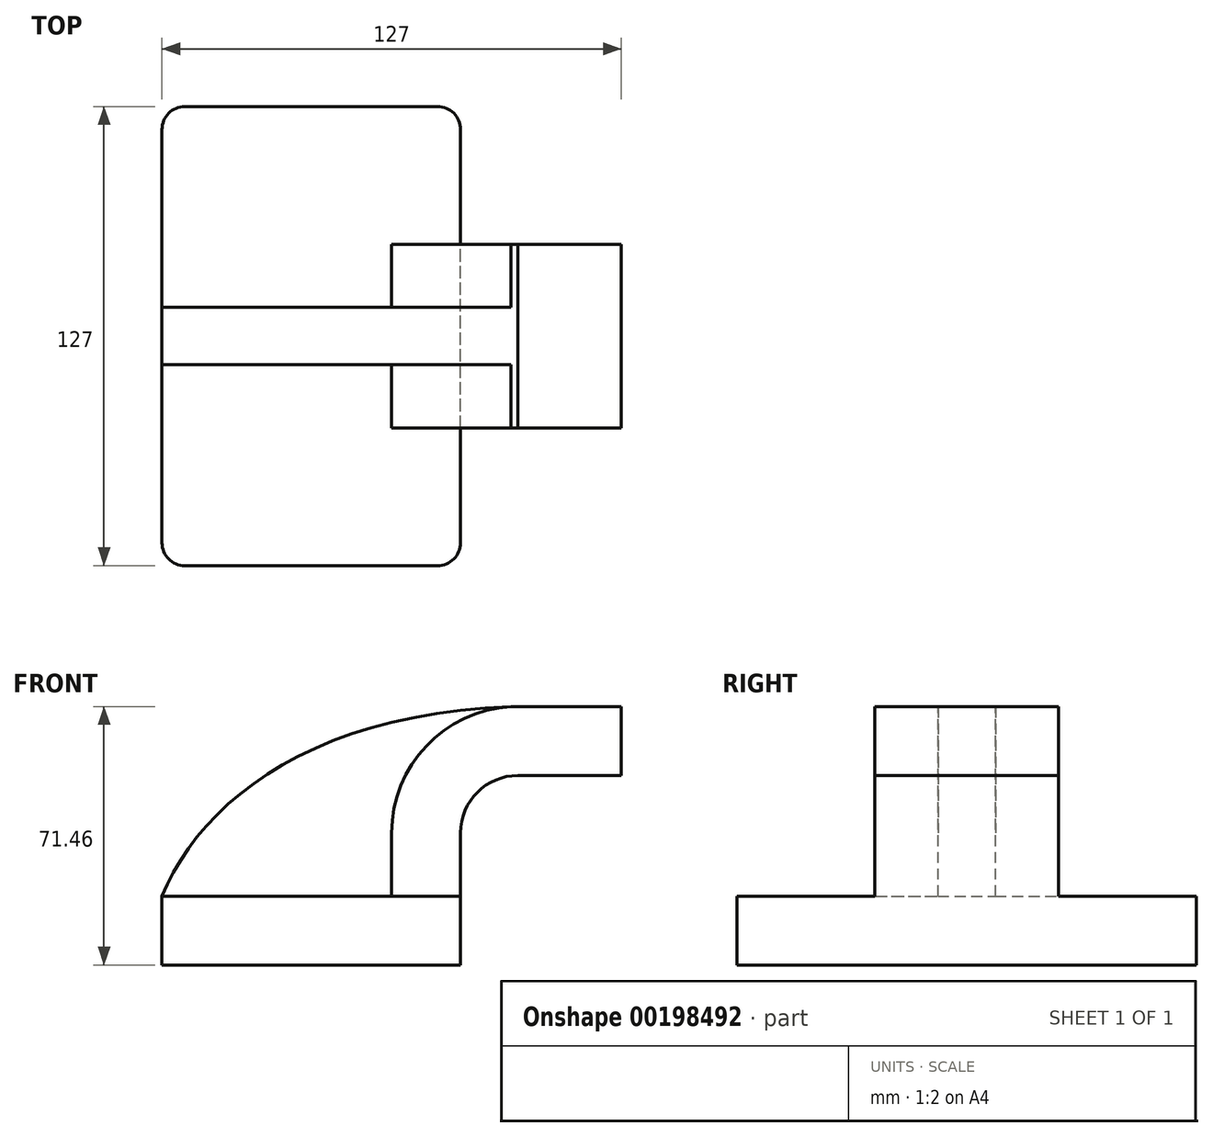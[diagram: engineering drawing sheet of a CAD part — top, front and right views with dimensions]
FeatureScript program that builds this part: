
annotation { "Feature Type Name" : "Feature", "Feature Type Description" : "" }
export const myFeature = defineFeature(function(context is Context, id is Id, definition is map)
    precondition{}
    {
        {
            var Q0;
            Q0=qCreatedBy(makeId("Front.planeOp"),FACE);
            var sketch = newSketch(context, id + "F0", { "sketchPlane" : qUnion([Q0])});
            skLineSegment(sketch, "E0.bottom", {"start": v(41.27, 9.53) * mm, "end": v(-41.28, 9.53) * mm});
            skLineSegment(sketch, "E0.top", {"start": v(41.28, -9.52) * mm, "end": v(-41.27, -9.52) * mm});
            skLineSegment(sketch, "E0.left", {"start": v(41.28, 9.53) * mm, "end": v(41.28, -9.52) * mm});
            skLineSegment(sketch, "E0.right", {"start": v(-41.28, 9.53) * mm, "end": v(-41.27, -9.52) * mm});
            skPoint(sketch, "E0.middle", {"position": v(0, 0) * mm});
            skLineSegment(sketch, "E1.bottom", {"start": v(111.13, 66.68) * mm, "end": v(60.33, 66.68) * mm});
            skLineSegment(sketch, "E1.top", {"start": v(111.13, 38.1) * mm, "end": v(60.33, 38.1) * mm});
            skLineSegment(sketch, "E1.left", {"start": v(111.13, 66.67) * mm, "end": v(111.13, 38.1) * mm});
            skLineSegment(sketch, "E1.right", {"start": v(60.33, 66.67) * mm, "end": v(60.33, 38.1) * mm});
            skPoint(sketch, "E1.middle", {"position": v(85.73, 52.39) * mm});
            skLineSegment(sketch, "E2", {"start": v(41.27, 9.53) * mm, "end": v(41.27, 27) * mm});
            skArc(sketch, "E3", {"start": v(41.27, 27) * mm, "mid": v(45.92, 38.23) * mm, "end": v(57.15, 42.88) * mm});
            skLineSegment(sketch, "E4", {"start": v(57.15, 42.88) * mm, "end": v(85.73, 42.88) * mm});
            skLineSegment(sketch, "E5.0", {"start": v(57.15, 61.93) * mm, "end": v(85.73, 61.93) * mm});
            skArc(sketch, "E5.1", {"start": v(22.23, 27) * mm, "mid": v(32.45, 51.7) * mm, "end": v(57.15, 61.93) * mm});
            skLineSegment(sketch, "E5.2", {"start": v(22.23, 9.53) * mm, "end": v(22.23, 27) * mm});
            skLineSegment(sketch, "E6", {"start": v(85.73, 66.68) * mm, "end": v(85.73, 38.1) * mm});
            skFitSpline(sketch, "E7", {"points": [v(-41.28, 9.53) * mm, v(57.15, 61.93) * mm], "startDerivative": vector(31.72, 77.02) * mm, "endDerivative": vector(171.45, 3.87) * mm});
            skSolve(sketch);
        }
        {
            var Q0;
            Q0=makeQuery(id+"F0.imprint","IMPRINT",FACE,{"disambiguationData":[TD([[makeQuery(id+"F0.imprint","IMPRINT",EDGE,{"derivedFrom":sQuery(id+"F0.wireOp",EDGE,"E0.top")}),-1.0]])]});
            extrude(context, id + "F1", {"entities" : qUnion([Q0]), "depth" : 127 * mm, "symmetric" : true});
        }
        {
            var Q0;
            {var subQ1=sQuery(id+"F0.wireOp",EDGE,"E2");Q0=makeQuery(id+"F0.imprint","IMPRINT",FACE,{"disambiguationData":[TD([[makeQuery(id+"F0.imprint","IMPRINT",EDGE,{"derivedFrom":subQ1}),1.0]])]});}
            extrude(context, id + "F2", {"entities" : qUnion([Q0]), "operationType" : NewBodyOperationType.ADD, "flatOperationType" : FlatOperationType.REMOVE, "offsetDistance" : 25.4 * mm, "depth" : 50.8 * mm, "domain" : OperationDomain.MODEL, "symmetric" : true});
        }
        {
            var Q0;
            {var subQ0=sQuery(id+"F0.wireOp",EDGE,"E5.0");var subQ1=sQuery(id+"F0.wireOp",EDGE,"E1.right");var subQ2=makeQuery(id+"F0.imprint","INTERSECT",VERTEX,{"derivedFrom":[subQ1,subQ0]});Q0=makeQuery(id+"F0.imprint","IMPRINT",FACE,{"disambiguationData":[TD([[makeQuery(id+"F0.imprint","IMPRINT",EDGE,{"disambiguationData":[TD([[subQ2,-1.0]])],"derivedFrom":subQ1}),1.0]])]});}
            extrude(context, id + "F3", {"entities" : qUnion([Q0]), "operationType" : NewBodyOperationType.ADD, "flatOperationType" : FlatOperationType.REMOVE, "offsetDistance" : 25.4 * mm, "depth" : 50.8 * mm, "domain" : OperationDomain.MODEL, "symmetric" : true});
        }
        {
            var Q0;
            {var subQ3=sQuery(id+"F0.wireOp",EDGE,"E5.2");Q0=makeQuery(id+"F0.imprint","IMPRINT",FACE,{"disambiguationData":[TD([[makeQuery(id+"F0.imprint","IMPRINT",EDGE,{"derivedFrom":subQ3}),1.0]])]});}
            extrude(context, id + "F4", {"entities" : qUnion([Q0]), "operationType" : NewBodyOperationType.ADD, "depth" : 15.88 * mm, "symmetric" : true});
        }
        {
            var Q0;
            Q0=makeQuery(id+"F1.opExtrude","CAP_EDGE",EDGE,{"disambiguationData":[OSD([sQuery(id+"F0.wireOp",EDGE,"E0.right")])],"isStart":false});
            var Q1;
            Q1=makeQuery(id+"F1.opExtrude","CAP_EDGE",EDGE,{"disambiguationData":[OSD([sQuery(id+"F0.wireOp",EDGE,"E0.left")])],"isStart":false});
            var Q2;
            Q2=makeQuery(id+"F1.opExtrude","CAP_EDGE",EDGE,{"disambiguationData":[OSD([sQuery(id+"F0.wireOp",EDGE,"E0.right")])],"isStart":true});
            var Q3;
            Q3=makeQuery(id+"F1.opExtrude","CAP_EDGE",EDGE,{"disambiguationData":[OSD([sQuery(id+"F0.wireOp",EDGE,"E0.left")])],"isStart":true});
            fillet(context, id + "F5", {"entities" : qUnion([Q0, Q1, Q2, Q3]), "radius" : 6.35 * mm, "tangentPropagation" : true, "allowEdgeOverflow" : false});
        }
    });
